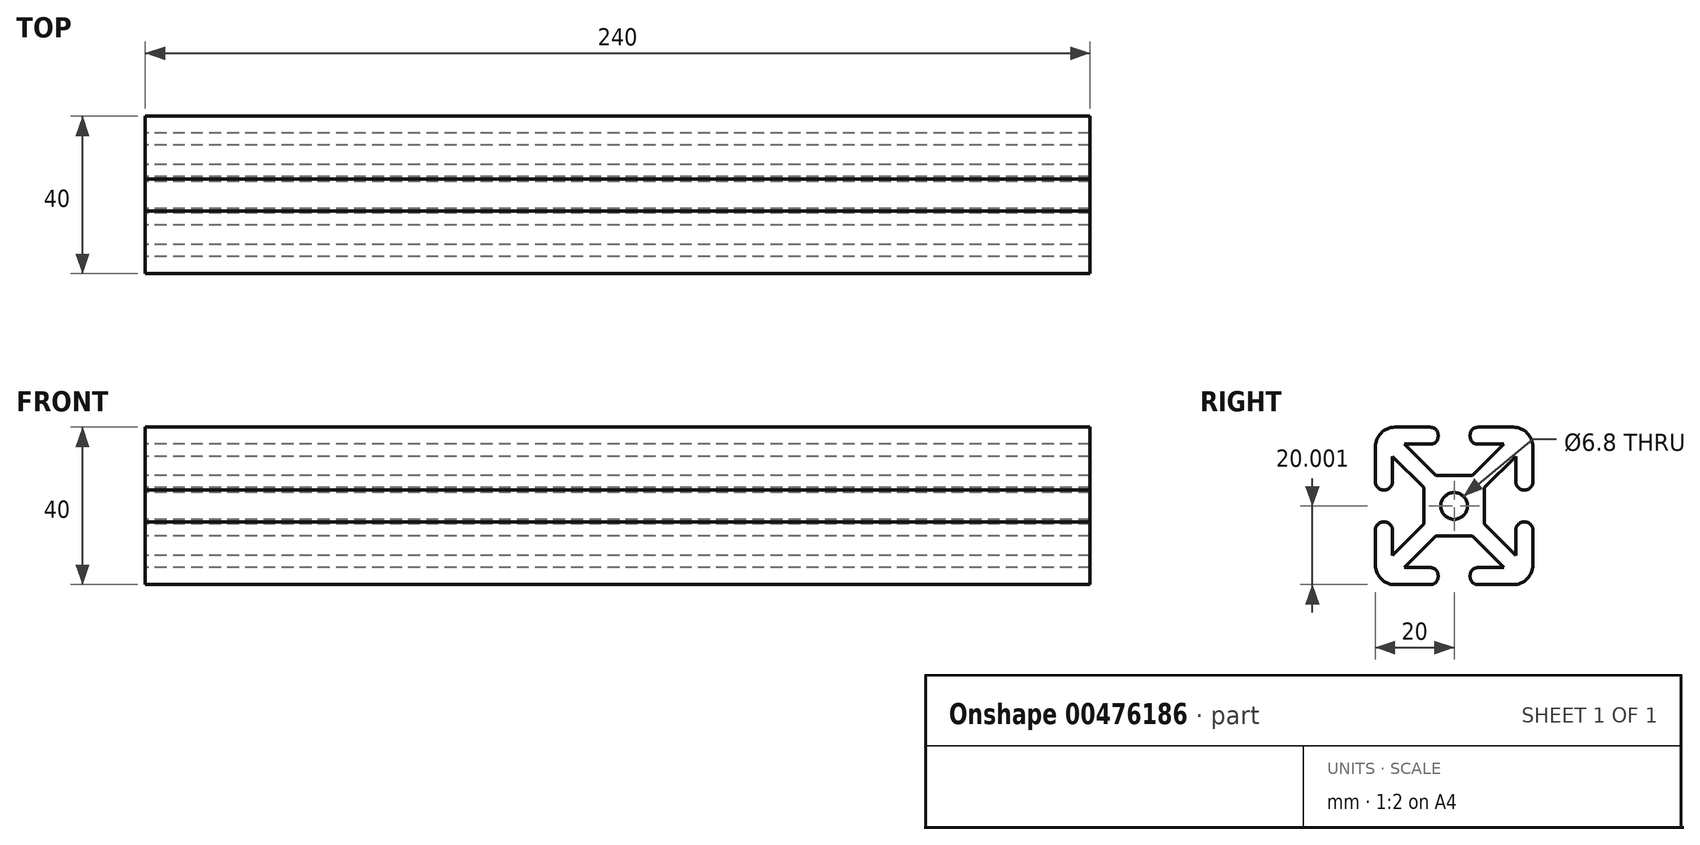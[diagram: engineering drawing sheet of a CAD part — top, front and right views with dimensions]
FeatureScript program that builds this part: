
annotation { "Feature Type Name" : "Feature", "Feature Type Description" : "" }
export const myFeature = defineFeature(function(context is Context, id is Id, definition is map)
    precondition{}
    {
        {
            var Q0;
            Q0=qCreatedBy(makeId("Right.planeOp"),FACE);
            var sketch = newSketch(context, id + "F0", { "sketchPlane" : qUnion([Q0])});
            skLineSegment(sketch, "E0", {"start": v(-15.94, 15.35) * mm, "end": v(0, 15.35) * mm});
            skLineSegment(sketch, "E1", {"start": v(0, 15.35) * mm, "end": v(8.12, 15.35) * mm, "construction": true});
            skLineSegment(sketch, "E2", {"start": v(8.12, 15.35) * mm, "end": v(24.06, 15.35) * mm});
            skLineSegment(sketch, "E3.bottom", {"start": v(-3.62, 3.04) * mm, "end": v(11.75, 3.04) * mm});
            skLineSegment(sketch, "E3.top", {"start": v(-3.62, -12.33) * mm, "end": v(11.75, -12.33) * mm});
            skLineSegment(sketch, "E3.left", {"start": v(-3.62, 3.04) * mm, "end": v(-3.62, -12.33) * mm});
            skLineSegment(sketch, "E3.right", {"start": v(11.75, 3.04) * mm, "end": v(11.75, -12.33) * mm});
            skLineSegment(sketch, "E4", {"start": v(11.74, 3.04) * mm, "end": v(24.06, 15.35) * mm, "construction": true});
            skLineSegment(sketch, "E5", {"start": v(-3.62, 3.04) * mm, "end": v(-15.94, 15.35) * mm});
            skLineSegment(sketch, "E6", {"start": v(-3.62, -12.33) * mm, "end": v(-15.94, -24.65) * mm, "construction": true});
            skLineSegment(sketch, "E7", {"start": v(11.74, -12.33) * mm, "end": v(24.06, -24.65) * mm});
            skLineSegment(sketch, "E8", {"start": v(16.5, 7.78) * mm, "end": v(14.97, 9.31) * mm, "construction": true});
            skLineSegment(sketch, "E9", {"start": v(16.5, 7.78) * mm, "end": v(18.02, 6.26) * mm, "construction": true});
            skLineSegment(sketch, "E10", {"start": v(14.97, 9.31) * mm, "end": v(21, 15.35) * mm});
            skLineSegment(sketch, "E11", {"start": v(18.02, 6.26) * mm, "end": v(24.06, 12.3) * mm});
            skLineSegment(sketch, "E12", {"start": v(14.97, 9.31) * mm, "end": v(-15.94, -21.6) * mm});
            skLineSegment(sketch, "E13", {"start": v(18.02, 6.26) * mm, "end": v(-12.89, -24.65) * mm});
            skLineSegment(sketch, "E14", {"start": v(0, 15.35) * mm, "end": v(0, 11.03) * mm});
            skLineSegment(sketch, "E15", {"start": v(8.12, 15.35) * mm, "end": v(8.12, 11.03) * mm});
            skLineSegment(sketch, "E16", {"start": v(8.12, 11.03) * mm, "end": v(16.69, 11.03) * mm});
            skLineSegment(sketch, "E17", {"start": v(0, 11.03) * mm, "end": v(-11.62, 11.03) * mm});
            skLineSegment(sketch, "E18", {"start": v(-3.62, 3.04) * mm, "end": v(11.75, -12.33) * mm});
            skLineSegment(sketch, "E19", {"start": v(11.74, 3.04) * mm, "end": v(-3.62, -12.33) * mm, "construction": true});
            skCircle(sketch, "E20", {"center": v(4.06, -4.65) * mm, "radius": 3.4 * mm});
            skLineSegment(sketch, "E21", {"start": v(24.06, -0.59) * mm, "end": v(24.06, -8.7) * mm, "construction": true});
            skLineSegment(sketch, "E22", {"start": v(24.06, -0.59) * mm, "end": v(24.06, 15.35) * mm});
            skLineSegment(sketch, "E23", {"start": v(24.06, -24.65) * mm, "end": v(24.06, -8.7) * mm});
            skLineSegment(sketch, "E24", {"start": v(24.06, -0.59) * mm, "end": v(19.74, -0.59) * mm});
            skLineSegment(sketch, "E25", {"start": v(24.06, -8.7) * mm, "end": v(19.74, -8.7) * mm});
            skLineSegment(sketch, "E26", {"start": v(19.74, -0.59) * mm, "end": v(19.74, 7.98) * mm});
            skLineSegment(sketch, "E27", {"start": v(19.74, 7.98) * mm, "end": v(16.69, 11.03) * mm});
            skLineSegment(sketch, "E28", {"start": v(-7.27, 6.68) * mm, "end": v(-8.8, 5.15) * mm});
            skLineSegment(sketch, "E29", {"start": v(-7.27, 6.68) * mm, "end": v(-5.74, 8.2) * mm});
            skLineSegment(sketch, "E30", {"start": v(-5.74, 8.2) * mm, "end": v(-12.89, 15.35) * mm});
            skLineSegment(sketch, "E31", {"start": v(-5.74, 8.2) * mm, "end": v(24.06, -21.6) * mm});
            skLineSegment(sketch, "E32", {"start": v(19.74, -8.7) * mm, "end": v(19.74, -17.27) * mm});
            skLineSegment(sketch, "E33", {"start": v(-15.94, 15.35) * mm, "end": v(-15.94, -0.59) * mm});
            skLineSegment(sketch, "E34", {"start": v(-15.94, -0.59) * mm, "end": v(-15.94, -8.7) * mm, "construction": true});
            skLineSegment(sketch, "E35", {"start": v(-15.94, -24.65) * mm, "end": v(0, -24.65) * mm});
            skLineSegment(sketch, "E36", {"start": v(0, -24.65) * mm, "end": v(8.12, -24.65) * mm, "construction": true});
            skLineSegment(sketch, "E37", {"start": v(-15.94, -8.7) * mm, "end": v(-15.94, -24.65) * mm});
            skLineSegment(sketch, "E38", {"start": v(8.12, -24.65) * mm, "end": v(24.06, -24.65) * mm});
            skLineSegment(sketch, "E39", {"start": v(-8.8, 5.15) * mm, "end": v(-15.94, 12.3) * mm});
            skLineSegment(sketch, "E40", {"start": v(-8.8, 5.15) * mm, "end": v(21, -24.65) * mm});
            skLineSegment(sketch, "E41", {"start": v(-15.94, -0.59) * mm, "end": v(-11.62, -0.59) * mm});
            skLineSegment(sketch, "E42", {"start": v(-15.94, -8.7) * mm, "end": v(-11.62, -8.7) * mm});
            skLineSegment(sketch, "E43", {"start": v(0, -24.65) * mm, "end": v(0, -20.33) * mm});
            skLineSegment(sketch, "E44", {"start": v(8.12, -24.65) * mm, "end": v(8.12, -20.33) * mm});
            skLineSegment(sketch, "E45", {"start": v(-11.62, -0.59) * mm, "end": v(-11.62, 7.98) * mm});
            skLineSegment(sketch, "E46", {"start": v(-11.62, -8.7) * mm, "end": v(-11.62, -17.27) * mm});
            skLineSegment(sketch, "E47", {"start": v(0, -20.33) * mm, "end": v(-8.57, -20.33) * mm});
            skLineSegment(sketch, "E48", {"start": v(8.12, -20.33) * mm, "end": v(16.69, -20.33) * mm});
            skSolve(sketch);
        }
        {
            var Q0;
            {var subQ0=sQuery(id+"F0.wireOp",EDGE,"E41");Q0=makeQuery(id+"F0.imprint","IMPRINT",FACE,{"disambiguationData":[TD([[makeQuery(id+"F0.imprint","IMPRINT",EDGE,{"derivedFrom":subQ0}),1.0]])]});}
            var Q1;
            {var subQ0=sQuery(id+"F0.wireOp",EDGE,"E28");Q1=makeQuery(id+"F0.imprint","IMPRINT",FACE,{"disambiguationData":[TD([[makeQuery(id+"F0.imprint","IMPRINT",EDGE,{"derivedFrom":subQ0}),-1.0]])]});}
            var Q2;
            {var subQ3=sQuery(id+"F0.wireOp",EDGE,"E29");Q2=makeQuery(id+"F0.imprint","IMPRINT",FACE,{"disambiguationData":[TD([[makeQuery(id+"F0.imprint","IMPRINT",EDGE,{"derivedFrom":subQ3}),1.0]])]});}
            var Q3;
            {var subQ0=sQuery(id+"F0.wireOp",EDGE,"E14");Q3=makeQuery(id+"F0.imprint","IMPRINT",FACE,{"disambiguationData":[TD([[makeQuery(id+"F0.imprint","IMPRINT",EDGE,{"derivedFrom":subQ0}),-1.0]])]});}
            var Q4;
            {var subQ0=sQuery(id+"F0.wireOp",EDGE,"E5");var subQ5=sQuery(id+"F0.wireOp",EDGE,"E17");var subQ6=makeQuery(id+"F0.imprint","INTERSECT",VERTEX,{"derivedFrom":[subQ0,subQ5]});Q4=makeQuery(id+"F0.imprint","IMPRINT",FACE,{"disambiguationData":[TD([[makeQuery(id+"F0.imprint","IMPRINT",EDGE,{"disambiguationData":[TD([[subQ6,1.0]])],"derivedFrom":subQ5}),-1.0]])]});}
            var Q5;
            {var subQ4=sQuery(id+"F0.wireOp",EDGE,"E42");Q5=makeQuery(id+"F0.imprint","IMPRINT",FACE,{"disambiguationData":[TD([[makeQuery(id+"F0.imprint","IMPRINT",EDGE,{"derivedFrom":subQ4}),-1.0]])]});}
            var Q6;
            {var subQ2=sQuery(id+"F0.wireOp",EDGE,"E3.left");var subQ6=sQuery(id+"F0.wireOp",EDGE,"E3.top");var subQ7=makeQuery(id+"F0.imprint","INTERSECT",VERTEX,{"derivedFrom":[subQ6,subQ2]});Q6=makeQuery(id+"F0.imprint","IMPRINT",FACE,{"disambiguationData":[TD([[makeQuery(id+"F0.imprint","IMPRINT",EDGE,{"disambiguationData":[TD([[subQ7,-1.0]])],"derivedFrom":subQ6}),-1.0]])]});}
            var Q7;
            {var subQ4=sQuery(id+"F0.wireOp",EDGE,"E43");Q7=makeQuery(id+"F0.imprint","IMPRINT",FACE,{"disambiguationData":[TD([[makeQuery(id+"F0.imprint","IMPRINT",EDGE,{"derivedFrom":subQ4}),1.0]])]});}
            var Q8;
            {var subQ3=sQuery(id+"F0.wireOp",EDGE,"E27");Q8=makeQuery(id+"F0.imprint","IMPRINT",FACE,{"disambiguationData":[TD([[makeQuery(id+"F0.imprint","IMPRINT",EDGE,{"derivedFrom":subQ3}),1.0]])]});}
            var Q9;
            {var subQ3=sQuery(id+"F0.wireOp",EDGE,"E27");Q9=makeQuery(id+"F0.imprint","IMPRINT",FACE,{"disambiguationData":[TD([[makeQuery(id+"F0.imprint","IMPRINT",EDGE,{"derivedFrom":subQ3}),-1.0]])]});}
            var Q10;
            {var subQ4=sQuery(id+"F0.wireOp",EDGE,"E24");Q10=makeQuery(id+"F0.imprint","IMPRINT",FACE,{"disambiguationData":[TD([[makeQuery(id+"F0.imprint","IMPRINT",EDGE,{"derivedFrom":subQ4}),-1.0]])]});}
            var Q11;
            {var subQ0=sQuery(id+"F0.wireOp",EDGE,"E15");Q11=makeQuery(id+"F0.imprint","IMPRINT",FACE,{"disambiguationData":[TD([[makeQuery(id+"F0.imprint","IMPRINT",EDGE,{"derivedFrom":subQ0}),1.0]])]});}
            var Q12;
            {var subQ0=sQuery(id+"F0.wireOp",EDGE,"E13");var subQ1=sQuery(id+"F0.wireOp",EDGE,"E3.right");var subQ2=makeQuery(id+"F0.imprint","INTERSECT",VERTEX,{"derivedFrom":[subQ1,subQ0]});Q12=makeQuery(id+"F0.imprint","IMPRINT",FACE,{"disambiguationData":[TD([[makeQuery(id+"F0.imprint","IMPRINT",EDGE,{"disambiguationData":[TD([[subQ2,-1.0]])],"derivedFrom":subQ1}),-1.0]])]});}
            var Q13;
            {var subQ0=sQuery(id+"F0.wireOp",EDGE,"E13");var subQ1=sQuery(id+"F0.wireOp",EDGE,"E3.top");var subQ2=makeQuery(id+"F0.imprint","INTERSECT",VERTEX,{"derivedFrom":[subQ1,subQ0]});Q13=makeQuery(id+"F0.imprint","IMPRINT",FACE,{"disambiguationData":[TD([[makeQuery(id+"F0.imprint","IMPRINT",EDGE,{"disambiguationData":[TD([[subQ2,-1.0]])],"derivedFrom":subQ1}),1.0]])]});}
            var Q14;
            {var subQ0=sQuery(id+"F0.wireOp",EDGE,"E40");var subQ1=sQuery(id+"F0.wireOp",EDGE,"E3.left");var subQ2=makeQuery(id+"F0.imprint","INTERSECT",VERTEX,{"derivedFrom":[subQ1,subQ0]});Q14=makeQuery(id+"F0.imprint","IMPRINT",FACE,{"disambiguationData":[TD([[makeQuery(id+"F0.imprint","IMPRINT",EDGE,{"disambiguationData":[TD([[subQ2,-1.0]])],"derivedFrom":subQ1}),1.0]])]});}
            var Q15;
            {var subQ0=sQuery(id+"F0.wireOp",EDGE,"E31");var subQ1=sQuery(id+"F0.wireOp",EDGE,"E3.bottom");var subQ2=makeQuery(id+"F0.imprint","INTERSECT",VERTEX,{"derivedFrom":[subQ1,subQ0]});Q15=makeQuery(id+"F0.imprint","IMPRINT",FACE,{"disambiguationData":[TD([[makeQuery(id+"F0.imprint","IMPRINT",EDGE,{"disambiguationData":[TD([[subQ2,-1.0]])],"derivedFrom":subQ1}),-1.0]])]});}
            var Q16;
            {var subQ5=sQuery(id+"F0.wireOp",EDGE,"E29");Q16=makeQuery(id+"F0.imprint","IMPRINT",FACE,{"disambiguationData":[TD([[makeQuery(id+"F0.imprint","IMPRINT",EDGE,{"derivedFrom":subQ5}),-1.0]])]});}
            var Q17;
            {var subQ5=sQuery(id+"F0.wireOp",EDGE,"E28");Q17=makeQuery(id+"F0.imprint","IMPRINT",FACE,{"disambiguationData":[TD([[makeQuery(id+"F0.imprint","IMPRINT",EDGE,{"derivedFrom":subQ5}),1.0]])]});}
            var Q18;
            {var subQ1=sQuery(id+"F0.wireOp",EDGE,"E7");Q18=makeQuery(id+"F0.imprint","IMPRINT",FACE,{"disambiguationData":[TD([[makeQuery(id+"F0.imprint","IMPRINT",EDGE,{"derivedFrom":subQ1}),-1.0]])]});}
            var Q19;
            {var subQ1=sQuery(id+"F0.wireOp",EDGE,"E7");Q19=makeQuery(id+"F0.imprint","IMPRINT",FACE,{"disambiguationData":[TD([[makeQuery(id+"F0.imprint","IMPRINT",EDGE,{"derivedFrom":subQ1}),1.0]])]});}
            var Q20;
            {var subQ0=sQuery(id+"F0.wireOp",EDGE,"E25");Q20=makeQuery(id+"F0.imprint","IMPRINT",FACE,{"disambiguationData":[TD([[makeQuery(id+"F0.imprint","IMPRINT",EDGE,{"derivedFrom":subQ0}),1.0]])]});}
            var Q21;
            {var subQ0=sQuery(id+"F0.wireOp",EDGE,"E44");Q21=makeQuery(id+"F0.imprint","IMPRINT",FACE,{"disambiguationData":[TD([[makeQuery(id+"F0.imprint","IMPRINT",EDGE,{"derivedFrom":subQ0}),-1.0]])]});}
            var Q22;
            {var subQ1=sQuery(id+"F0.wireOp",EDGE,"E3.right");var subQ6=sQuery(id+"F0.wireOp",EDGE,"E3.bottom");var subQ9=makeQuery(id+"F0.imprint","INTERSECT",VERTEX,{"derivedFrom":[subQ6,subQ1]});Q22=makeQuery(id+"F0.imprint","IMPRINT",FACE,{"disambiguationData":[TD([[makeQuery(id+"F0.imprint","IMPRINT",EDGE,{"disambiguationData":[TD([[subQ9,1.0]])],"derivedFrom":subQ6}),-1.0]])]});}
            var Q23;
            {var subQ0=sQuery(id+"F0.wireOp",EDGE,"E18");var subQ5=sQuery(id+"F0.wireOp",EDGE,"E20");var subQ6=makeQuery(id+"F0.imprint","INTERSECT",VERTEX,{"disambiguationData":[OD(0.0)],"derivedFrom":[subQ0,subQ5]});Q23=makeQuery(id+"F0.imprint","IMPRINT",FACE,{"disambiguationData":[TD([[makeQuery(id+"F0.imprint","IMPRINT",EDGE,{"disambiguationData":[TD([[subQ6,-1.0]])],"derivedFrom":subQ5}),-1.0]])]});}
            var Q24;
            {var subQ1=sQuery(id+"F0.wireOp",EDGE,"E3.top");var subQ6=sQuery(id+"F0.wireOp",EDGE,"E3.left");var subQ9=makeQuery(id+"F0.imprint","INTERSECT",VERTEX,{"derivedFrom":[subQ1,subQ6]});Q24=makeQuery(id+"F0.imprint","IMPRINT",FACE,{"disambiguationData":[TD([[makeQuery(id+"F0.imprint","IMPRINT",EDGE,{"disambiguationData":[TD([[subQ9,-1.0]])],"derivedFrom":subQ1}),1.0]])]});}
            var Q25;
            {var subQ0=sQuery(id+"F0.wireOp",EDGE,"E18");var subQ5=sQuery(id+"F0.wireOp",EDGE,"E20");var subQ6=makeQuery(id+"F0.imprint","INTERSECT",VERTEX,{"disambiguationData":[OD(1.0)],"derivedFrom":[subQ0,subQ5]});Q25=makeQuery(id+"F0.imprint","IMPRINT",FACE,{"disambiguationData":[TD([[makeQuery(id+"F0.imprint","IMPRINT",EDGE,{"disambiguationData":[TD([[subQ6,1.0]])],"derivedFrom":subQ5}),-1.0]])]});}
            var Q26;
            {var subQ0=sQuery(id+"F0.wireOp",EDGE,"E18");var subQ5=sQuery(id+"F0.wireOp",EDGE,"E20");var subQ6=makeQuery(id+"F0.imprint","INTERSECT",VERTEX,{"disambiguationData":[OD(1.0)],"derivedFrom":[subQ0,subQ5]});Q26=makeQuery(id+"F0.imprint","IMPRINT",FACE,{"disambiguationData":[TD([[makeQuery(id+"F0.imprint","IMPRINT",EDGE,{"disambiguationData":[TD([[subQ6,-1.0]])],"derivedFrom":subQ5}),-1.0]])]});}
            var Q27;
            {var subQ0=sQuery(id+"F0.wireOp",EDGE,"E18");var subQ5=sQuery(id+"F0.wireOp",EDGE,"E20");var subQ6=makeQuery(id+"F0.imprint","INTERSECT",VERTEX,{"disambiguationData":[OD(0.0)],"derivedFrom":[subQ0,subQ5]});Q27=makeQuery(id+"F0.imprint","IMPRINT",FACE,{"disambiguationData":[TD([[makeQuery(id+"F0.imprint","IMPRINT",EDGE,{"disambiguationData":[TD([[subQ6,1.0]])],"derivedFrom":subQ5}),-1.0]])]});}
            extrude(context, id + "F1", {"entities" : qUnion([Q0, Q1, Q2, Q3, Q4, Q5, Q6, Q7, Q8, Q9, Q10, Q11, Q12, Q13, Q14, Q15, Q16, Q17, Q18, Q19, Q20, Q21, Q22, Q23, Q24, Q25, Q26, Q27]), "depth" : 240 * mm, "offsetDistance" : 25 * mm});
        }
        {
            var Q0;
            Q0=makeQuery(id+"F1.opExtrude","SWEPT_EDGE",EDGE,{"disambiguationData":[OSD([sQuery(id+"F0.wireOp",EDGE,"E14"),sQuery(id+"F0.wireOp",EDGE,"E17")])]});
            var Q1;
            Q1=makeQuery(id+"F1.opExtrude","SWEPT_EDGE",EDGE,{"disambiguationData":[OSD([sQuery(id+"F0.wireOp",EDGE,"E41"),sQuery(id+"F0.wireOp",EDGE,"E45")])]});
            var Q2;
            Q2=makeQuery(id+"F1.opExtrude","SWEPT_EDGE",EDGE,{"disambiguationData":[OSD([sQuery(id+"F0.wireOp",EDGE,"E33"),sQuery(id+"F0.wireOp",EDGE,"E41")])]});
            var Q3;
            Q3=makeQuery(id+"F1.opExtrude","SWEPT_EDGE",EDGE,{"disambiguationData":[OSD([sQuery(id+"F0.wireOp",EDGE,"E0"),sQuery(id+"F0.wireOp",EDGE,"E14")])]});
            var Q4;
            Q4=makeQuery(id+"F1.opExtrude","SWEPT_EDGE",EDGE,{"disambiguationData":[OSD([sQuery(id+"F0.wireOp",EDGE,"E15"),sQuery(id+"F0.wireOp",EDGE,"E16")])]});
            var Q5;
            Q5=makeQuery(id+"F1.opExtrude","SWEPT_EDGE",EDGE,{"disambiguationData":[OSD([sQuery(id+"F0.wireOp",EDGE,"E24"),sQuery(id+"F0.wireOp",EDGE,"E26")])]});
            var Q6;
            Q6=makeQuery(id+"F1.opExtrude","SWEPT_EDGE",EDGE,{"disambiguationData":[OSD([sQuery(id+"F0.wireOp",EDGE,"E22"),sQuery(id+"F0.wireOp",EDGE,"E24")])]});
            var Q7;
            Q7=makeQuery(id+"F1.opExtrude","SWEPT_EDGE",EDGE,{"disambiguationData":[OSD([sQuery(id+"F0.wireOp",EDGE,"E38"),sQuery(id+"F0.wireOp",EDGE,"E44")])]});
            var Q8;
            Q8=makeQuery(id+"F1.opExtrude","SWEPT_EDGE",EDGE,{"disambiguationData":[OSD([sQuery(id+"F0.wireOp",EDGE,"E2"),sQuery(id+"F0.wireOp",EDGE,"E15")])]});
            var Q9;
            Q9=makeQuery(id+"F1.opExtrude","SWEPT_EDGE",EDGE,{"disambiguationData":[OSD([sQuery(id+"F0.wireOp",EDGE,"E37"),sQuery(id+"F0.wireOp",EDGE,"E42")])]});
            var Q10;
            Q10=makeQuery(id+"F1.opExtrude","SWEPT_EDGE",EDGE,{"disambiguationData":[OSD([sQuery(id+"F0.wireOp",EDGE,"E42"),sQuery(id+"F0.wireOp",EDGE,"E46")])]});
            var Q11;
            Q11=makeQuery(id+"F1.opExtrude","SWEPT_EDGE",EDGE,{"disambiguationData":[OSD([sQuery(id+"F0.wireOp",EDGE,"E35"),sQuery(id+"F0.wireOp",EDGE,"E43")])]});
            var Q12;
            Q12=makeQuery(id+"F1.opExtrude","SWEPT_EDGE",EDGE,{"disambiguationData":[OSD([sQuery(id+"F0.wireOp",EDGE,"E43"),sQuery(id+"F0.wireOp",EDGE,"E47")])]});
            var Q13;
            Q13=makeQuery(id+"F1.opExtrude","SWEPT_EDGE",EDGE,{"disambiguationData":[OSD([sQuery(id+"F0.wireOp",EDGE,"E44"),sQuery(id+"F0.wireOp",EDGE,"E48")])]});
            var Q14;
            Q14=makeQuery(id+"F1.opExtrude","SWEPT_EDGE",EDGE,{"disambiguationData":[OSD([sQuery(id+"F0.wireOp",EDGE,"E25"),sQuery(id+"F0.wireOp",EDGE,"E32")])]});
            var Q15;
            Q15=makeQuery(id+"F1.opExtrude","SWEPT_EDGE",EDGE,{"disambiguationData":[OSD([sQuery(id+"F0.wireOp",EDGE,"E23"),sQuery(id+"F0.wireOp",EDGE,"E25")])]});
            fillet(context, id + "F2", {"entities" : qUnion([Q0, Q1, Q2, Q3, Q4, Q5, Q6, Q7, Q8, Q9, Q10, Q11, Q12, Q13, Q14, Q15]), "radius" : 2 * mm, "tangentPropagation" : true, "allowEdgeOverflow" : false});
        }
        {
            var Q0;
            Q0=makeQuery(id+"F1.opExtrude","SWEPT_EDGE",EDGE,{"disambiguationData":[OSD([sQuery(id+"F0.wireOp",EDGE,"E0"),sQuery(id+"F0.wireOp",EDGE,"E5"),sQuery(id+"F0.wireOp",EDGE,"E33")])]});
            var Q1;
            Q1=makeQuery(id+"F1.opExtrude","SWEPT_EDGE",EDGE,{"disambiguationData":[OSD([sQuery(id+"F0.wireOp",EDGE,"E2"),sQuery(id+"F0.wireOp",EDGE,"E22")])]});
            var Q2;
            Q2=makeQuery(id+"F1.opExtrude","SWEPT_EDGE",EDGE,{"disambiguationData":[OSD([sQuery(id+"F0.wireOp",EDGE,"E7"),sQuery(id+"F0.wireOp",EDGE,"E23"),sQuery(id+"F0.wireOp",EDGE,"E38")])]});
            var Q3;
            Q3=makeQuery(id+"F1.opExtrude","SWEPT_EDGE",EDGE,{"disambiguationData":[OSD([sQuery(id+"F0.wireOp",EDGE,"E35"),sQuery(id+"F0.wireOp",EDGE,"E37")])]});
            fillet(context, id + "F3", {"entities" : qUnion([Q0, Q1, Q2, Q3]), "radius" : 5 * mm, "tangentPropagation" : true, "allowEdgeOverflow" : false});
        }
    });
